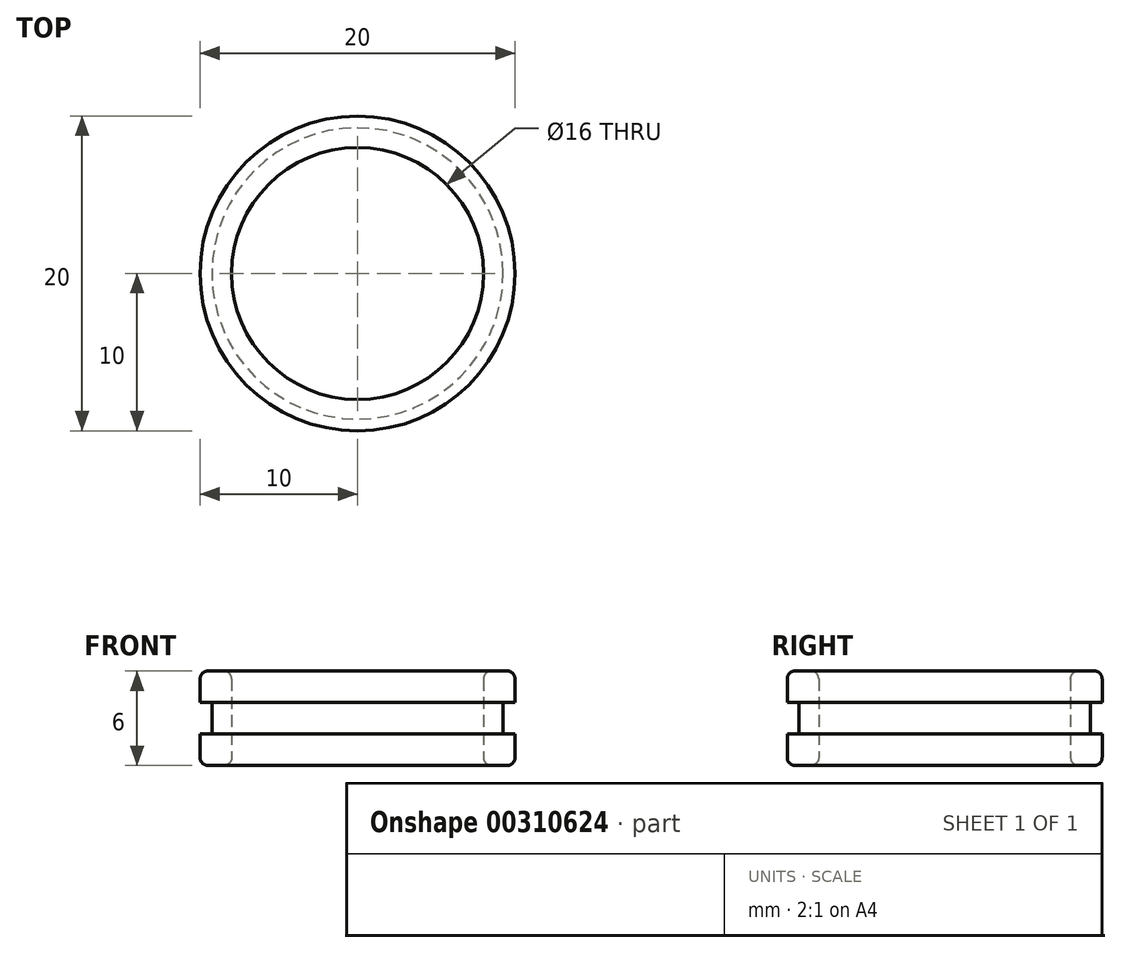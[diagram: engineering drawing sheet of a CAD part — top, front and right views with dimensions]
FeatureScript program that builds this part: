
annotation { "Feature Type Name" : "Feature", "Feature Type Description" : "" }
export const myFeature = defineFeature(function(context is Context, id is Id, definition is map)
    precondition{}
    {
        {
            var Q0;
            Q0=qCreatedBy(makeId("Top.planeOp"),FACE);
            var sketch = newSketch(context, id + "F0", { "sketchPlane" : qUnion([Q0])});
            skCircle(sketch, "E0", {"center": v(0, 0) * mm, "radius": 10 * mm});
            skCircle(sketch, "E1", {"center": v(0, 0) * mm, "radius": 8 * mm});
            skCircle(sketch, "E2", {"center": v(0, 0) * mm, "radius": 9.25 * mm});
            skSolve(sketch);
        }
        {
            var Q0;
            Q0=makeQuery(id+"F0.imprint","IMPRINT",FACE,{"disambiguationData":[TD([[makeQuery(id+"F0.imprint","IMPRINT",EDGE,{"derivedFrom":sQuery(id+"F0.wireOp",EDGE,"E0")}),1.0]])]});
            var Q1;
            Q1=makeQuery(id+"F0.imprint","IMPRINT",FACE,{"disambiguationData":[TD([[makeQuery(id+"F0.imprint","IMPRINT",EDGE,{"derivedFrom":sQuery(id+"F0.wireOp",EDGE,"E1")}),-1.0]])]});
            extrude(context, id + "F1", {"entities" : qUnion([Q0, Q1]), "endBound" : BoundingType.SYMMETRIC, "depth" : 6 * mm});
        }
        {
            var Q0;
            Q0 = qSketchRegion(id + "F0", true);
            extrude(context, id + "F2", {"entities" : qUnion([Q0]), "operationType" : NewBodyOperationType.REMOVE, "endBound" : BoundingType.SYMMETRIC, "oppositeDirection" : true, "depth" : 2 * mm});
        }
        {
            var Q0;
            Q0=makeQuery(id+"F1.opExtrude","CAP_EDGE",EDGE,{"disambiguationData":[OSD([sQuery(id+"F0.wireOp",EDGE,"E0")])],"isStart":false});
            var Q1;
            Q1=makeQuery(id+"F1.opExtrude","CAP_EDGE",EDGE,{"disambiguationData":[OSD([sQuery(id+"F0.wireOp",EDGE,"E1")])],"isStart":false});
            var Q2;
            Q2=makeQuery(id+"F1.opExtrude","CAP_EDGE",EDGE,{"disambiguationData":[OSD([sQuery(id+"F0.wireOp",EDGE,"E0")])],"isStart":true});
            var Q3;
            Q3=makeQuery(id+"F1.opExtrude","CAP_EDGE",EDGE,{"disambiguationData":[OSD([sQuery(id+"F0.wireOp",EDGE,"E1")])],"isStart":true});
            fillet(context, id + "F3", {"entities" : qUnion([Q0, Q1, Q2, Q3]), "radius" : 0.5 * mm, "tangentPropagation" : true, "allowEdgeOverflow" : false});
        }
    });
